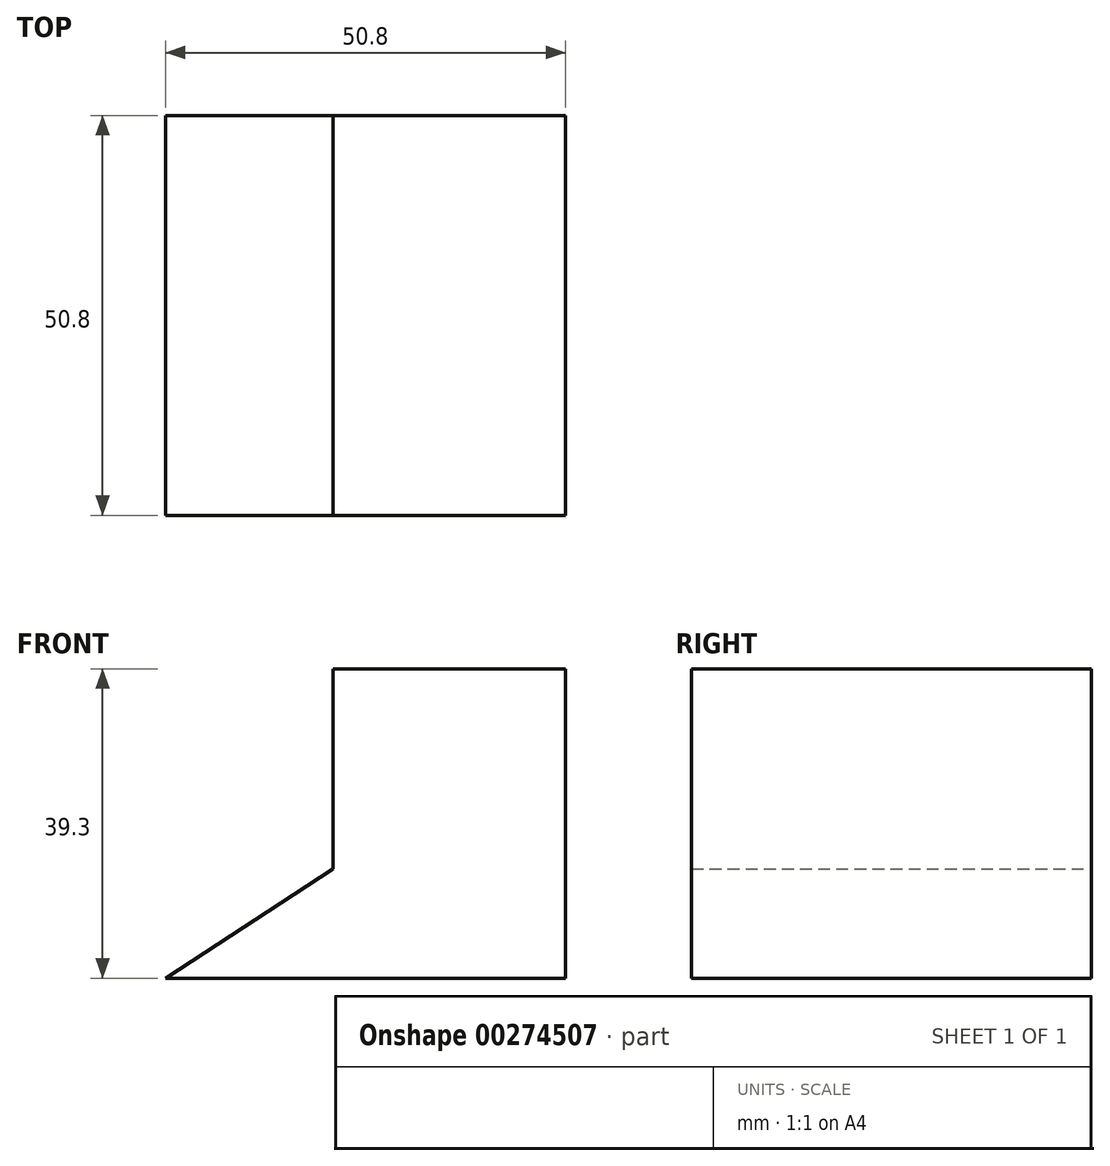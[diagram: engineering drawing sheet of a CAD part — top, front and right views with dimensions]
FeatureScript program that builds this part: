
annotation { "Feature Type Name" : "Feature", "Feature Type Description" : "" }
export const myFeature = defineFeature(function(context is Context, id is Id, definition is map)
    precondition{}
    {
        {
            var Q0;
            Q0=qCreatedBy(makeId("Front.planeOp"),FACE);
            var sketch = newSketch(context, id + "F0", { "sketchPlane" : qUnion([Q0])});
            skLineSegment(sketch, "E0", {"start": v(0, 0) * mm, "end": v(-50.8, 0) * mm});
            skLineSegment(sketch, "E1", {"start": v(-50.8, 0) * mm, "end": v(-29.54, 13.9) * mm});
            skLineSegment(sketch, "E2", {"start": v(-29.54, 13.9) * mm, "end": v(-29.54, 39.3) * mm});
            skLineSegment(sketch, "E3", {"start": v(-29.54, 39.3) * mm, "end": v(0, 39.3) * mm});
            skLineSegment(sketch, "E4", {"start": v(0, 39.3) * mm, "end": v(0, 0) * mm});
            skSolve(sketch);
        }
        {
            var Q0;
            Q0=makeQuery(id+"F0.imprint","IMPRINT",FACE,{"disambiguationData":[TD([[makeQuery(id+"F0.imprint","IMPRINT",EDGE,{"derivedFrom":sQuery(id+"F0.wireOp",EDGE,"E0")}),-1.0]])]});
            extrude(context, id + "F1", {"entities" : qUnion([Q0]), "depth" : 50.8 * mm});
        }
    });
